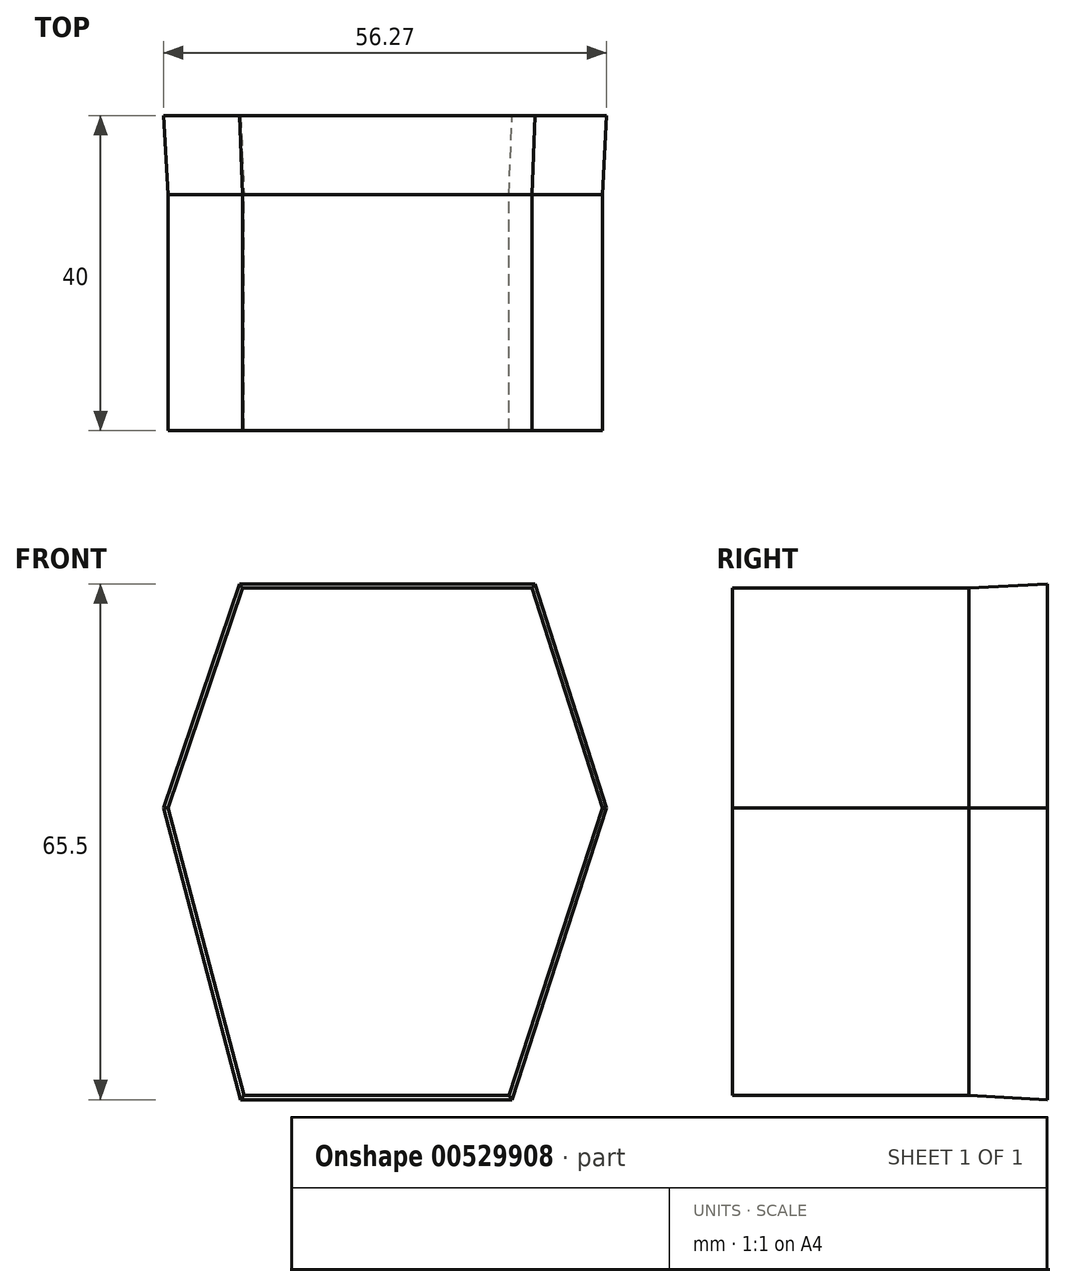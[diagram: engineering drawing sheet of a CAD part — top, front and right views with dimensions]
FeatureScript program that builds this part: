
annotation { "Feature Type Name" : "Feature", "Feature Type Description" : "" }
export const myFeature = defineFeature(function(context is Context, id is Id, definition is map)
    precondition{}
    {
        {
            var Q0;
            Q0=qCreatedBy(makeId("Front.planeOp"),FACE);
            var sketch = newSketch(context, id + "F0", { "sketchPlane" : qUnion([Q0])});
            skLineSegment(sketch, "E0", {"start": v(-27.04, 0) * mm, "end": v(-17.57, 27.95) * mm});
            skLineSegment(sketch, "E1", {"start": v(-17.57, 27.95) * mm, "end": v(19.2, 27.95) * mm});
            skLineSegment(sketch, "E2", {"start": v(19.2, 27.95) * mm, "end": v(28.13, 0) * mm});
            skLineSegment(sketch, "E3", {"start": v(28.13, 0) * mm, "end": v(16.3, -36.5) * mm});
            skLineSegment(sketch, "E4", {"start": v(16.3, -36.5) * mm, "end": v(0, -36.5) * mm});
            skLineSegment(sketch, "E5", {"start": v(0, -36.5) * mm, "end": v(-17.39, -36.5) * mm});
            skLineSegment(sketch, "E6", {"start": v(-27.04, 0) * mm, "end": v(-17.39, -36.5) * mm});
            skSolve(sketch);
        }
        {
            var Q0;
            Q0 = qSketchRegion(id + "F0", true);
            extrude(context, id + "F1", {"entities" : qUnion([Q0]), "depth" : 30 * mm, "offsetDistance" : 25 * mm, "hasSecondDirection" : true, "secondDirectionOppositeDirection" : true, "secondDirectionDepth" : 10 * mm, "hasSecondDirectionDraft" : true, "secondDirectionDraftAngle" : 3 * degree});
        }
    });
